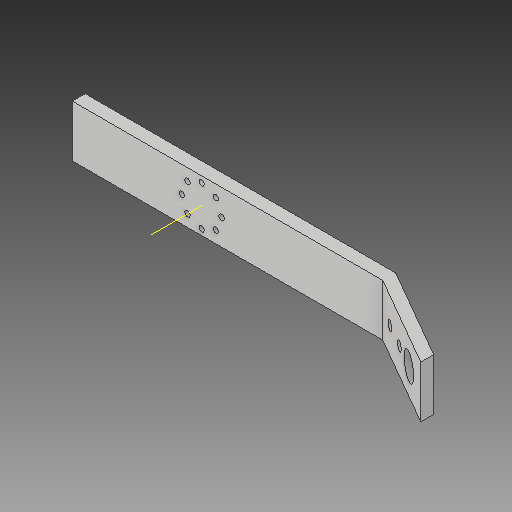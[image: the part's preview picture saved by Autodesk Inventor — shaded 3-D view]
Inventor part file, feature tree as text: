
AUTODESK INVENTOR PART (.ipt)
format: ipt  version: 2019 (Build 230136000, 136)  size: 163,840 bytes
history: native  units: in
note: dims shown in document units (in); Inventor stores cm internally (conversion verified against a paired STEP export)
features: sketch x4, extrude x3, hole x1, other x1
ambient origin geometry x8: Origin, YZ Plane, XZ Plane, XY Plane, X Axis, Y Axis, Z Axis, Center Point
bodies: Solid1 (feature_tree)
feature tree (9):
  extrude  "Extrusion1"  Depth=1.0in
  sketch  "Sketch4"  dims[d2=0.25in d3=0.0in d53=2.0in]
  extrude  "Extrusion9"  Depth=0.25in
  extrude  "Extrusion10"  Depth=2.0in
  hole  "Hole1"  [1 undecoded]
  other  "Work Axis1"
  sketch  "Sketch1"  dims[d0=6.0in d1=1.0in]
  sketch  "Sketch9"  dims[d54=30.0deg d55=2.0in]
  sketch  "Sketch10"  dims[d56=30.0deg d57=1.0in d58=0.0in d59=1.0in d60=0.5in d61=0.5in d62=0.5in d63=0.5in d64=1.0in d65=1.5in d66=0.184in d67=0.184in d68=0.5in d69=1.0in d70=0.0in d71=0.107in d72=0.385in d73=0.0in d74=3.1496in d76=360.0deg d78=0.107in d79=0.236in d80=0.375in d81=0.25in d82=0.5635in d83=1.0in d84=0.8108in d85=1.0in d86=0.5in d87=3.5in]
note: 1 required parameter value undecoded (feature->parameter linkage not recoverable at this tier; creation-order binding heuristic only, values carry confidence <= 0.55)
